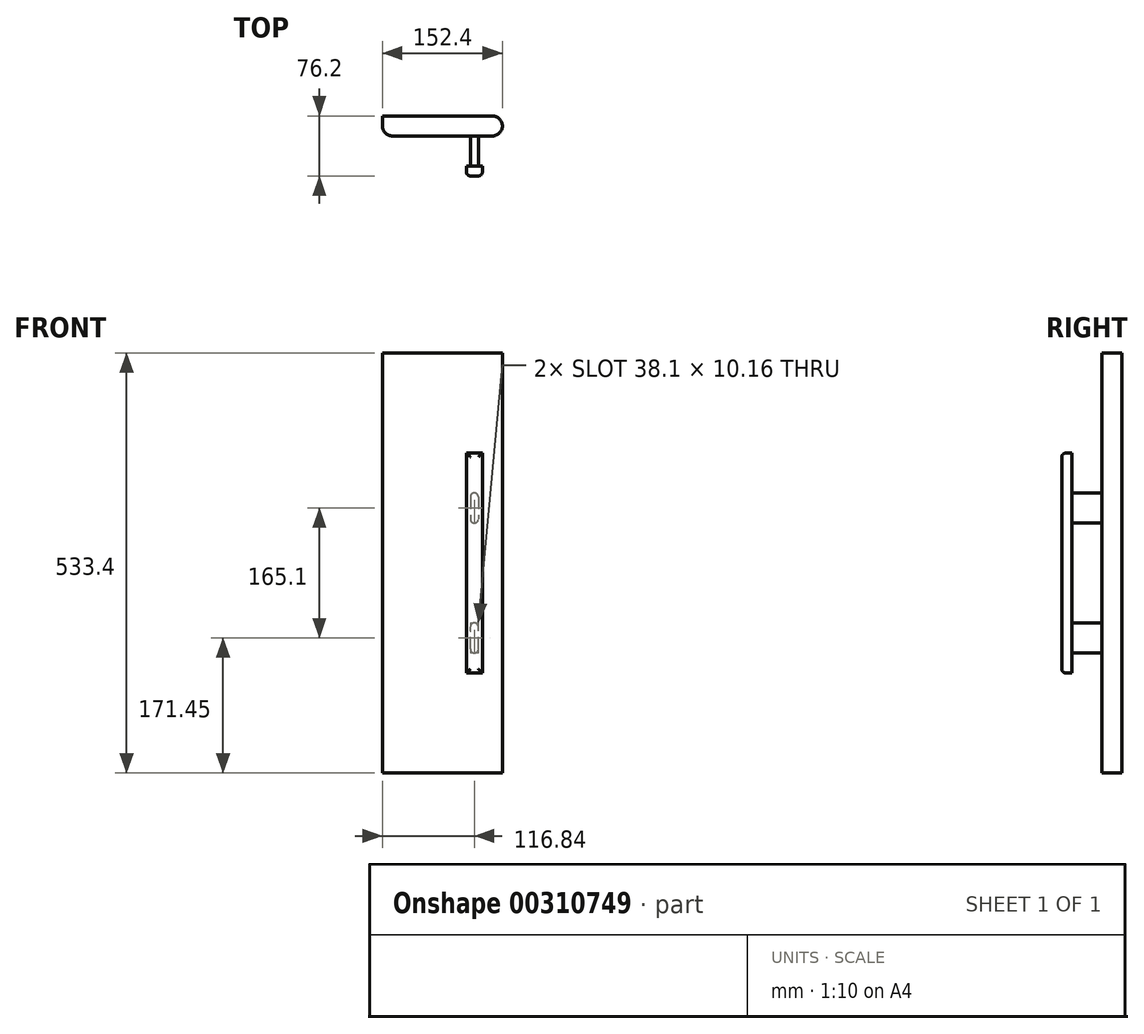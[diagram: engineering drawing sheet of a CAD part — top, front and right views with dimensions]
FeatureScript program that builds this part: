
annotation { "Feature Type Name" : "Feature", "Feature Type Description" : "" }
export const myFeature = defineFeature(function(context is Context, id is Id, definition is map)
    precondition{}
    {
        {
            var Q0;
            Q0=qCreatedBy(makeId("Top.planeOp"),FACE);
            var sketch = newSketch(context, id + "F0", { "sketchPlane" : qUnion([Q0])});
            skLineSegment(sketch, "E0.bottom", {"start": v(-76.2, 25.4) * mm, "end": v(63.5, 25.4) * mm});
            skLineSegment(sketch, "E0.top", {"start": v(-63.5, 0) * mm, "end": v(63.5, 0) * mm});
            skLineSegment(sketch, "E0.left", {"start": v(-76.2, 25.4) * mm, "end": v(-76.2, 12.7) * mm});
            skLineSegment(sketch, "E0.right", {"start": v(76.2, 12.7) * mm, "end": v(76.2, 12.7) * mm});
            skPoint(sketch, "E1.visualSharp", {"position": v(-76.2, 0) * mm});
            skArc(sketch, "E1.filletArc", {"start": v(-76.2, 12.7) * mm, "mid": v(-72.48, 3.72) * mm, "end": v(-63.5, 0) * mm});
            skPoint(sketch, "E2.visualSharp", {"position": v(76.2, 25.4) * mm});
            skArc(sketch, "E2.filletArc", {"start": v(76.2, 12.7) * mm, "mid": v(72.48, 21.68) * mm, "end": v(63.5, 25.4) * mm});
            skPoint(sketch, "E3.visualSharp", {"position": v(76.2, 0) * mm});
            skArc(sketch, "E3.filletArc", {"start": v(63.5, 0) * mm, "mid": v(72.48, 3.72) * mm, "end": v(76.2, 12.7) * mm});
            skSolve(sketch);
        }
        {
            var Q0;
            Q0 = qSketchRegion(id + "F0", true);
            extrude(context, id + "F1", {"entities" : qUnion([Q0]), "depth" : 533.4 * mm});
        }
        {
            var Q0;
            Q0=makeQuery(id+"F1.opExtrude","SWEPT_FACE",FACE,{"disambiguationData":[OSD([sQuery(id+"F0.wireOp",EDGE,"E0.top")])]});
            cPlane(context, id + "F2", {"entities" : qUnion([Q0]), "cplaneType" : CPlaneType.OFFSET, "offset" : 38.1 * mm, "width" : 152.4 * mm, "height" : 152.4 * mm});
        }
        {
            var Q0;
            Q0=qCreatedBy(id+"F2.planeOp",FACE);
            var sketch = newSketch(context, id + "F3", { "sketchPlane" : qUnion([Q0])});
            skLineSegment(sketch, "E4.bottom", {"start": v(30.48, 406.4) * mm, "end": v(50.8, 406.4) * mm});
            skLineSegment(sketch, "E4.top", {"start": v(30.48, 127) * mm, "end": v(50.8, 127) * mm});
            skLineSegment(sketch, "E4.left", {"start": v(30.48, 406.4) * mm, "end": v(30.48, 127) * mm});
            skLineSegment(sketch, "E4.right", {"start": v(50.8, 406.4) * mm, "end": v(50.8, 127) * mm});
            skSolve(sketch);
        }
        {
            var Q0;
            Q0=makeQuery(id+"F1.opExtrude","SWEPT_FACE",FACE,{"disambiguationData":[OSD([sQuery(id+"F0.wireOp",EDGE,"E0.top")])]});
            var sketch = newSketch(context, id + "F4", { "sketchPlane" : qUnion([Q0])});
            skLineSegment(sketch, "E5.bottom", {"start": v(35.56, 355.6) * mm, "end": v(45.72, 355.6) * mm});
            skLineSegment(sketch, "E5.top", {"start": v(35.56, 317.5) * mm, "end": v(45.72, 317.5) * mm});
            skLineSegment(sketch, "E5.left", {"start": v(35.56, 355.6) * mm, "end": v(35.56, 317.5) * mm});
            skLineSegment(sketch, "E6.MirrorCS", {"start": v(35.56, 190.5) * mm, "end": v(45.72, 190.5) * mm});
            skLineSegment(sketch, "E7.MirrorCS", {"start": v(45.72, 152.4) * mm, "end": v(45.72, 190.5) * mm});
            skLineSegment(sketch, "E8.MirrorCS", {"start": v(35.56, 152.4) * mm, "end": v(45.72, 152.4) * mm});
            skLineSegment(sketch, "E9.MirrorCS", {"start": v(35.56, 152.4) * mm, "end": v(35.56, 190.5) * mm});
            skLineSegment(sketch, "E10", {"start": v(45.72, 355.6) * mm, "end": v(45.72, 317.5) * mm});
            skSolve(sketch);
        }
        {
            var Q0;
            Q0 = qSketchRegion(id + "F4", true);
            var Q1;
            Q1=qCreatedBy(id+"F2.planeOp",FACE);
            extrude(context, id + "F5", {"entities" : qUnion([Q0]), "operationType" : NewBodyOperationType.ADD, "endBound" : BoundingType.UP_TO_SURFACE, "endBoundEntityFace" : qUnion([Q1]), "depth" : 25.4 * mm});
        }
        {
            var Q0;
            Q0=makeQuery(id+"F5.opExtrude","SWEPT_EDGE",EDGE,{"disambiguationData":[OSD([sQuery(id+"F4.wireOp",EDGE,"E5.bottom"),sQuery(id+"F4.wireOp",EDGE,"E5.left")])]});
            var Q1;
            Q1=makeQuery(id+"F5.opExtrude","SWEPT_EDGE",EDGE,{"disambiguationData":[OSD([sQuery(id+"F4.wireOp",EDGE,"E5.bottom"),sQuery(id+"F4.wireOp",EDGE,"E10")])]});
            var Q2;
            Q2=makeQuery(id+"F5.opExtrude","SWEPT_EDGE",EDGE,{"disambiguationData":[OSD([sQuery(id+"F4.wireOp",EDGE,"E5.top"),sQuery(id+"F4.wireOp",EDGE,"E10")])]});
            var Q3;
            Q3=makeQuery(id+"F5.opExtrude","SWEPT_EDGE",EDGE,{"disambiguationData":[OSD([sQuery(id+"F4.wireOp",EDGE,"E5.top"),sQuery(id+"F4.wireOp",EDGE,"E5.left")])]});
            var Q4;
            Q4=makeQuery(id+"F5.opExtrude","SWEPT_EDGE",EDGE,{"disambiguationData":[OSD([sQuery(id+"F4.wireOp",EDGE,"E6.MirrorCS"),sQuery(id+"F4.wireOp",EDGE,"E9.MirrorCS")])]});
            var Q5;
            Q5=makeQuery(id+"F5.opExtrude","SWEPT_EDGE",EDGE,{"disambiguationData":[OSD([sQuery(id+"F4.wireOp",EDGE,"E6.MirrorCS"),sQuery(id+"F4.wireOp",EDGE,"E7.MirrorCS")])]});
            var Q6;
            Q6=makeQuery(id+"F5.opExtrude","SWEPT_EDGE",EDGE,{"disambiguationData":[OSD([sQuery(id+"F4.wireOp",EDGE,"E8.MirrorCS"),sQuery(id+"F4.wireOp",EDGE,"E9.MirrorCS")])]});
            var Q7;
            Q7=makeQuery(id+"F5.opExtrude","SWEPT_EDGE",EDGE,{"disambiguationData":[OSD([sQuery(id+"F4.wireOp",EDGE,"E7.MirrorCS"),sQuery(id+"F4.wireOp",EDGE,"E8.MirrorCS")])]});
            fillet(context, id + "F6", {"entities" : qUnion([Q0, Q1, Q2, Q3, Q4, Q5, Q6, Q7]), "radius" : 5.08 * mm, "tangentPropagation" : true, "allowEdgeOverflow" : false});
        }
        {
            var Q0;
            Q0 = qSketchRegion(id + "F3", true);
            extrude(context, id + "F7", {"entities" : qUnion([Q0]), "operationType" : NewBodyOperationType.ADD, "depth" : 12.7 * mm});
        }
        {
            var Q0;
            Q0=makeQuery(id+"F7.opExtrude","CAP_EDGE",EDGE,{"disambiguationData":[OSD([sQuery(id+"F3.wireOp",EDGE,"E4.bottom")])],"isStart":false});
            var Q1;
            Q1=makeQuery(id+"F7.opExtrude","CAP_EDGE",EDGE,{"disambiguationData":[OSD([sQuery(id+"F3.wireOp",EDGE,"E4.left")])],"isStart":false});
            var Q2;
            Q2=makeQuery(id+"F7.opExtrude","CAP_EDGE",EDGE,{"disambiguationData":[OSD([sQuery(id+"F3.wireOp",EDGE,"E4.right")])],"isStart":false});
            var Q3;
            Q3=makeQuery(id+"F7.opExtrude","CAP_EDGE",EDGE,{"disambiguationData":[OSD([sQuery(id+"F3.wireOp",EDGE,"E4.top")])],"isStart":false});
            fillet(context, id + "F8", {"entities" : qUnion([Q0, Q1, Q2, Q3]), "radius" : 5.08 * mm, "tangentPropagation" : true, "allowEdgeOverflow" : false});
        }
    });
